# Revit family: OxEquip - Wall Compatible Outlet
name_source: partatom
category: Electrical Fixtures
revit_build: Autodesk Revit 2018 (Build: 20180423_1000(x64)
units: mm (PartAtom-declared; Revit-internal decimal feet)

## family parameters
Always vertical = No
Cut with Voids When Loaded = No
Maintain Annotation Orientation = No
Part Type = Normal
Room Calculation Point = No
Round Connector Dimension = Use Diameter
Shared = Yes
Work Plane-Based = Yes

## types (3) — shared parameters
Default Elevation = 1219.2 mm  [stored 4 ft]
Description = Amico Alert-1 Series Outlet
Face Plate = Amico_Stainless_Steel [Wall Outlet]
GWB (Thickness) = 16 mm  [stored 0.0524934 ft]
Manufacturer = Amico Pipeline
Pastic = Amico_White Plastic
Pipe = Copper
Pipe Length = 200 mm  [stored 0.656168 ft]
URL = http://www.amico.com

## per-type parameters (varying)
| type | A | Gas Type | Model | O | Pipe I.D. | Pipe O.D. | V |
| Medical Air | Yes | [PB]MedAir [Wall Outlet] | O-OXWAL-U-AIR | No | 13.375 mm  [stored 0.0438812 ft] | 15.875 mm | No |
| MedVac | No | [PB]MedVac [Wall Outlet] | O-OXWAL-U-VAC | No | 19.725 mm | 22.225 mm | Yes |
| Oxygen | No | [PB]Oxygen [Wall Outlet] | O-OXWAL-U-OXY | Yes | 13.375 mm  [stored 0.0438812 ft] | 15.875 mm | No |

note: [stored X ft] marks values corroborated as IEEE doubles in the binary element streams (Revit-internal decimal feet)

## geometry (parser evidence)
native form markers: Blend x2, Sweep x4
no freeform markers — native parametric forms only
